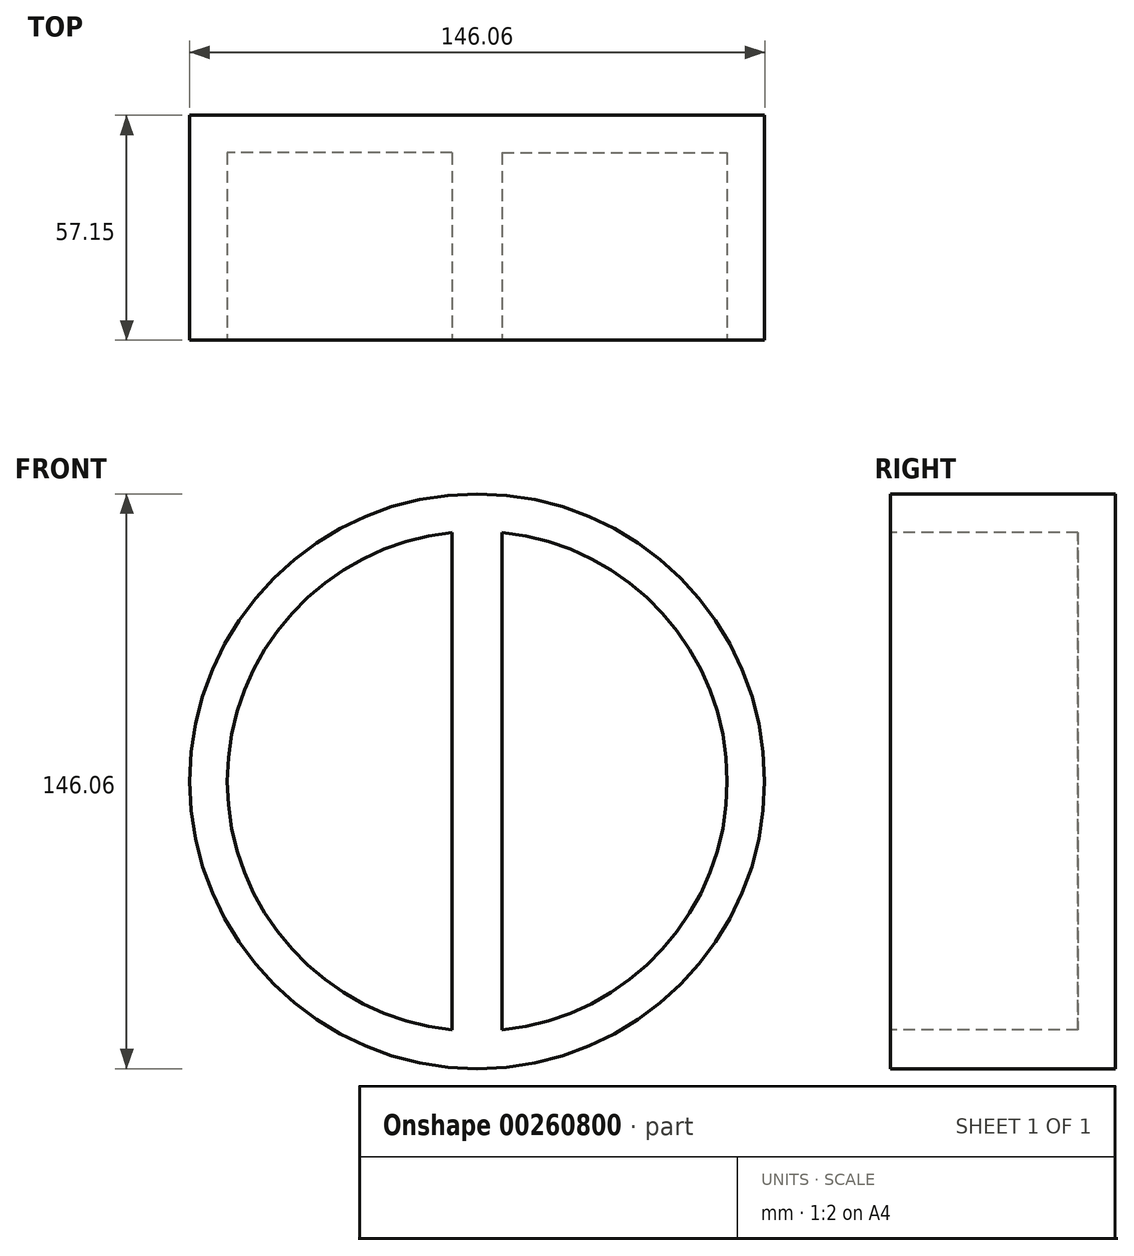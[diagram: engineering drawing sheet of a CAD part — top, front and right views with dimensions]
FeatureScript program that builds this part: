
annotation { "Feature Type Name" : "Feature", "Feature Type Description" : "" }
export const myFeature = defineFeature(function(context is Context, id is Id, definition is map)
    precondition{}
    {
        {
            var Q0;
            Q0=qCreatedBy(makeId("Front.planeOp"),FACE);
            var sketch = newSketch(context, id + "F0", { "sketchPlane" : qUnion([Q0])});
            skCircle(sketch, "E0", {"center": v(0, 0) * mm, "radius": 73.03 * mm});
            skLineSegment(sketch, "E1", {"start": v(0, 0) * mm, "end": v(-6.35, 0) * mm});
            skLineSegment(sketch, "E2", {"start": v(0, 0) * mm, "end": v(6.35, 0) * mm});
            skLineSegment(sketch, "E3", {"start": v(-6.35, 72.75) * mm, "end": v(-6.35, -72.75) * mm});
            skLineSegment(sketch, "E4", {"start": v(6.35, 72.75) * mm, "end": v(6.35, -72.75) * mm});
            skSolve(sketch);
        }
        {
            var Q0;
            Q0=qCreatedBy(makeId("Front.planeOp"),FACE);
            var sketch = newSketch(context, id + "F1", { "sketchPlane" : qUnion([Q0])});
            skCircle(sketch, "E5", {"center": v(0, 0) * mm, "radius": 63.5 * mm});
            skSolve(sketch);
        }
        {
            var Q0;
            {var subQ0=sQuery(id+"F0.wireOp",EDGE,"E3");var subQ1=sQuery(id+"F0.wireOp",EDGE,"E0");var subQ2=makeQuery(id+"F0.imprint","INTERSECT",VERTEX,{"disambiguationData":[OD(0.0)],"derivedFrom":[subQ1,subQ0]});Q0=makeQuery(id+"F0.imprint","IMPRINT",FACE,{"disambiguationData":[TD([[makeQuery(id+"F0.imprint","IMPRINT",EDGE,{"disambiguationData":[TD([[subQ2,-1.0]])],"derivedFrom":subQ1}),1.0]])]});}
            var Q1;
            {var subQ0=sQuery(id+"F0.wireOp",EDGE,"E4");var subQ1=sQuery(id+"F0.wireOp",EDGE,"E0");var subQ2=makeQuery(id+"F0.imprint","INTERSECT",VERTEX,{"disambiguationData":[OD(0.0)],"derivedFrom":[subQ1,subQ0]});Q1=makeQuery(id+"F0.imprint","IMPRINT",FACE,{"disambiguationData":[TD([[makeQuery(id+"F0.imprint","IMPRINT",EDGE,{"disambiguationData":[TD([[subQ2,1.0]])],"derivedFrom":subQ1}),1.0]])]});}
            var Q2;
            {var subQ1=sQuery(id+"F0.wireOp",EDGE,"E1");Q2=makeQuery(id+"F0.imprint","IMPRINT",FACE,{"disambiguationData":[TD([[makeQuery(id+"F0.imprint","IMPRINT",EDGE,{"derivedFrom":subQ1}),-1.0]])]});}
            var Q3;
            {var subQ1=sQuery(id+"F0.wireOp",EDGE,"E1");Q3=makeQuery(id+"F0.imprint","IMPRINT",FACE,{"disambiguationData":[TD([[makeQuery(id+"F0.imprint","IMPRINT",EDGE,{"derivedFrom":subQ1}),1.0]])]});}
            extrude(context, id + "F2", {"entities" : qUnion([Q0, Q1, Q2, Q3]), "oppositeDirection" : true, "depth" : 57.15 * mm});
        }
        {
            var Q0;
            Q0=makeQuery(id+"F1.imprint","IMPRINT",FACE,{"disambiguationData":[TD([[makeQuery(id+"F1.imprint","IMPRINT",EDGE,{"derivedFrom":sQuery(id+"F1.wireOp",EDGE,"E5")}),1.0]])]});
            extrude(context, id + "F3", {"entities" : qUnion([Q0]), "operationType" : NewBodyOperationType.REMOVE, "oppositeDirection" : true, "depth" : 47.62 * mm});
        }
        {
            var Q0;
            {var subQ1=sQuery(id+"F0.wireOp",EDGE,"E1");Q0=makeQuery(id+"F0.imprint","IMPRINT",FACE,{"disambiguationData":[TD([[makeQuery(id+"F0.imprint","IMPRINT",EDGE,{"derivedFrom":subQ1}),1.0]])]});}
            var Q1;
            {var subQ1=sQuery(id+"F0.wireOp",EDGE,"E1");Q1=makeQuery(id+"F0.imprint","IMPRINT",FACE,{"disambiguationData":[TD([[makeQuery(id+"F0.imprint","IMPRINT",EDGE,{"derivedFrom":subQ1}),-1.0]])]});}
            extrude(context, id + "F4", {"entities" : qUnion([Q0, Q1]), "operationType" : NewBodyOperationType.ADD, "oppositeDirection" : true, "depth" : 47.62 * mm});
        }
    });
